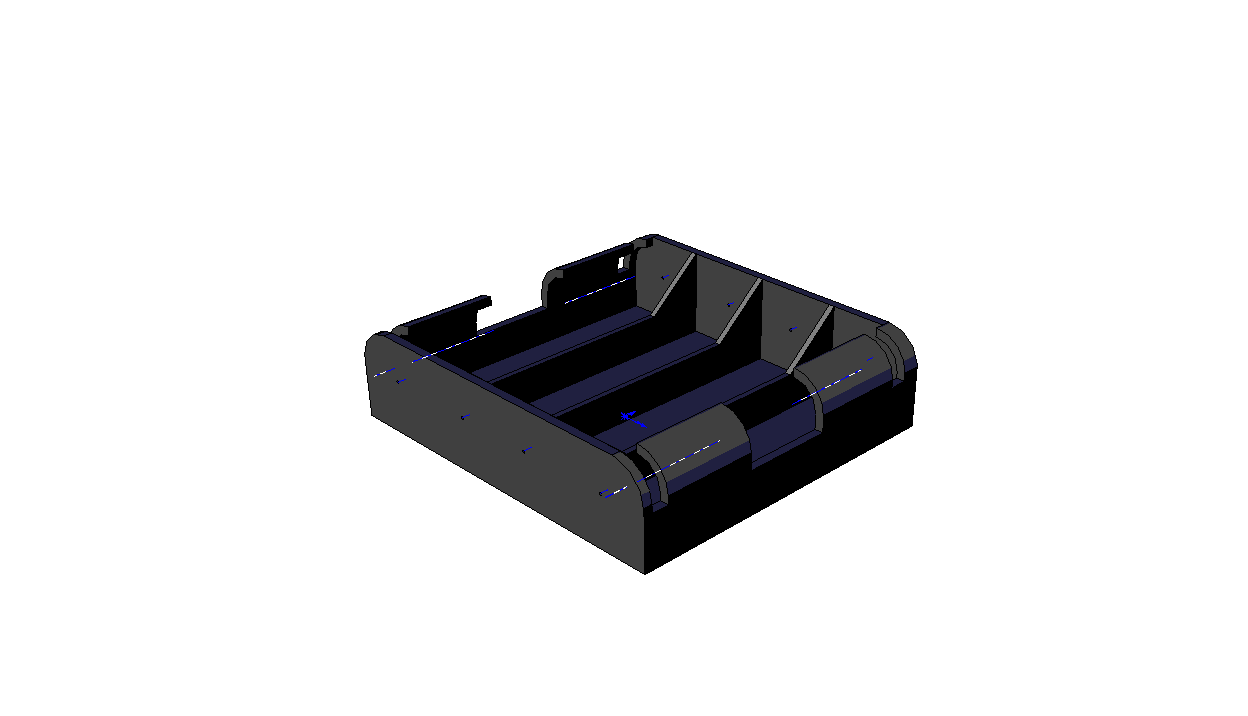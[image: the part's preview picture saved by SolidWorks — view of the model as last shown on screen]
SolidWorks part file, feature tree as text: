
SOLIDWORKS PART (.sldprt)
format: sldprt  version: not decoded by parser v0  size: 268,800 bytes
history: native  units: mm
features: sketch x6, extrude x5, plane x3, material x1, fillet x1, shell x1, cut_extrude x1 (+8 scaffold rows collapsed)
feature tree (26):
  scaffold x8  (default folders/planes/origin — collapsed)
  material  "Matériau <non spécifié>"
  plane  "Face"
  plane  "Dessus"
  plane  "Droite"
  sketch  "Esquisse1"  dims[D1=1.5mm D2=58.0mm D3=63.0mm D4=50.0mm]
  extrude  "Base-Extrusion"  Depth=16mm
  fillet  "Congé1"  Radius=6mm
  shell  "Coque1"  Thickness=1.5mm
  sketch  "Esquisse3"
  cut_extrude  "Enlèv. mat.-Extru.2"  [1 undecoded]
  sketch  "Esquisse7"  dims[D1=31.5mm D2=15.3mm D3=15.3mm D4=0.5mm D5=0.5mm D6=1.0mm]
  extrude  "Extrusion2"  Depth=14.5mm
  sketch  "Esquisse8"  dims[D1=7.5mm D2=10.0mm D3=29.0mm]
  extrude  "Enlèv. mat.-Extru.5"  Depth=35mm
  sketch  "Esquisse10"  dims[D4=2.0mm D1=7.0mm D2=8.5mm D3=38.5mm]
  extrude  "Enlèv. mat.-Extru.6"  [1 undecoded]
  sketch  "Esquisse11"  dims[D4=2.0mm D1=7.0mm D2=8.5mm D3=38.5mm]
  extrude  "Enlèv. mat.-Extru.7"  [1 undecoded]
decode coverage: 10 of 14 modeling features carry decoded parameters
note: 3 parameter values undecoded
summary: no parameter record found for 3 features
note: suppression state not decoded; provenance and decode notes live in map.json
